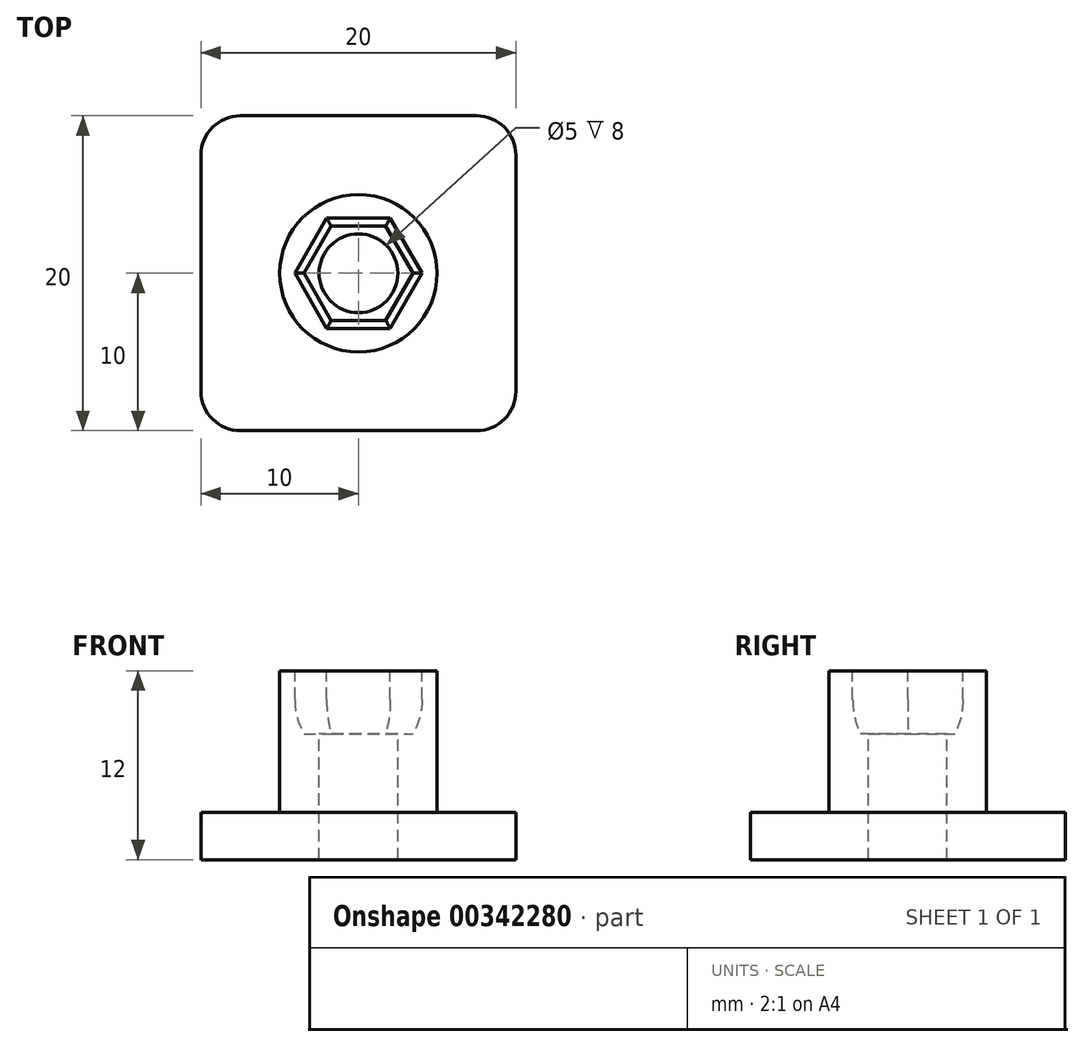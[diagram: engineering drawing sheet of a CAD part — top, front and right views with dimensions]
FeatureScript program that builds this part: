
annotation { "Feature Type Name" : "Feature", "Feature Type Description" : "" }
export const myFeature = defineFeature(function(context is Context, id is Id, definition is map)
    precondition{}
    {
        {
            var Q0;
            Q0=qCreatedBy(makeId("Top.planeOp"),FACE);
            var sketch = newSketch(context, id + "F0", { "sketchPlane" : qUnion([Q0])});
            skLineSegment(sketch, "E0.bottom", {"start": v(7.5, 10) * mm, "end": v(-7.5, 10) * mm});
            skLineSegment(sketch, "E0.top", {"start": v(7.5, -10) * mm, "end": v(-7.5, -10) * mm});
            skLineSegment(sketch, "E0.left", {"start": v(10, 7.5) * mm, "end": v(10, -7.5) * mm});
            skLineSegment(sketch, "E0.right", {"start": v(-10, 7.5) * mm, "end": v(-10, -7.5) * mm});
            skPoint(sketch, "E0.middle", {"position": v(0, 0) * mm});
            skPoint(sketch, "E1.visualSharp", {"position": v(-10, 10) * mm});
            skArc(sketch, "E1.filletArc", {"start": v(-7.5, 10) * mm, "mid": v(-9.27, 9.27) * mm, "end": v(-10, 7.5) * mm});
            skPoint(sketch, "E2.visualSharp", {"position": v(10, 10) * mm});
            skArc(sketch, "E2.filletArc", {"start": v(10, 7.5) * mm, "mid": v(9.27, 9.27) * mm, "end": v(7.5, 10) * mm});
            skPoint(sketch, "E3.visualSharp", {"position": v(10, -10) * mm});
            skArc(sketch, "E3.filletArc", {"start": v(7.5, -10) * mm, "mid": v(9.27, -9.27) * mm, "end": v(10, -7.5) * mm});
            skPoint(sketch, "E4.visualSharp", {"position": v(-10, -10) * mm});
            skArc(sketch, "E4.filletArc", {"start": v(-10, -7.5) * mm, "mid": v(-9.27, -9.27) * mm, "end": v(-7.5, -10) * mm});
            skSolve(sketch);
        }
        {
            var Q0;
            Q0=makeQuery(id+"F0.imprint","IMPRINT",FACE,{"disambiguationData":[TD([[makeQuery(id+"F0.imprint","IMPRINT",EDGE,{"derivedFrom":sQuery(id+"F0.wireOp",EDGE,"E0.bottom")}),1.0]])]});
            extrude(context, id + "F1", {"entities" : qUnion([Q0]), "depth" : 3 * mm});
        }
        {
            var Q0;
            Q0=makeQuery(id+"F1.opExtrude","CAP_FACE",FACE,{"disambiguationData":[OSD([sQuery(id+"F0.wireOp",EDGE,"E0.bottom"),sQuery(id+"F0.wireOp",EDGE,"E0.top"),sQuery(id+"F0.wireOp",EDGE,"E0.left"),sQuery(id+"F0.wireOp",EDGE,"E0.right"),sQuery(id+"F0.wireOp",EDGE,"E1.filletArc"),sQuery(id+"F0.wireOp",EDGE,"E2.filletArc"),sQuery(id+"F0.wireOp",EDGE,"E3.filletArc"),sQuery(id+"F0.wireOp",EDGE,"E4.filletArc")])],"isStart":false});
            var sketch = newSketch(context, id + "F2", { "sketchPlane" : qUnion([Q0])});
            skCircle(sketch, "E5", {"center": v(0, 0) * mm, "radius": 5 * mm});
            skSolve(sketch);
        }
        {
            var Q0;
            Q0=makeQuery(id+"F2.imprint","IMPRINT",FACE,{"disambiguationData":[TD([[makeQuery(id+"F2.imprint","IMPRINT",EDGE,{"derivedFrom":sQuery(id+"F2.wireOp",EDGE,"E5")}),1.0]])]});
            extrude(context, id + "F3", {"entities" : qUnion([Q0]), "operationType" : NewBodyOperationType.ADD, "depth" : 9 * mm});
        }
        {
            var Q0;
            Q0=makeQuery(id+"F3.opExtrude","CAP_FACE",FACE,{"disambiguationData":[OSD([sQuery(id+"F2.wireOp",EDGE,"E5")])],"isStart":false});
            var sketch = newSketch(context, id + "F4", { "sketchPlane" : qUnion([Q0])});
            skCircle(sketch, "E6.cCircle", {"center": v(0, 0) * mm, "radius": 3.5 * mm, "construction": true});
            skLineSegment(sketch, "E6.0", {"start": v(-2.02, 3.5) * mm, "end": v(2.02, 3.5) * mm});
            skLineSegment(sketch, "E6.1", {"start": v(2.02, 3.5) * mm, "end": v(4.04, 0) * mm});
            skLineSegment(sketch, "E6.2", {"start": v(4.04, 0) * mm, "end": v(2.02, -3.5) * mm});
            skLineSegment(sketch, "E6.3", {"start": v(2.02, -3.5) * mm, "end": v(-2.02, -3.5) * mm});
            skLineSegment(sketch, "E6.4", {"start": v(-2.02, -3.5) * mm, "end": v(-4.04, 0) * mm});
            skLineSegment(sketch, "E6.5", {"start": v(-4.04, 0) * mm, "end": v(-2.02, 3.5) * mm});
            skPoint(sketch, "E6.0.midPoint", {"position": v(0, 3.5) * mm});
            skSolve(sketch);
        }
        {
            var Q0;
            Q0=makeQuery(id+"F4.imprint","IMPRINT",FACE,{"disambiguationData":[TD([[makeQuery(id+"F4.imprint","IMPRINT",EDGE,{"derivedFrom":sQuery(id+"F4.wireOp",EDGE,"E6.0")}),-1.0]])]});
            extrude(context, id + "F5", {"entities" : qUnion([Q0]), "operationType" : NewBodyOperationType.REMOVE, "oppositeDirection" : true, "depth" : 4 * mm});
        }
        {
            var Q0;
            Q0=makeQuery(id+"F5.boolean.opBoolean","COPY",FACE,{"derivedFrom":makeQuery(id+"F5.opExtrude","CAP_FACE",FACE,{"disambiguationData":[OSD([sQuery(id+"F4.wireOp",EDGE,"E6.0"),sQuery(id+"F4.wireOp",EDGE,"E6.1"),sQuery(id+"F4.wireOp",EDGE,"E6.2"),sQuery(id+"F4.wireOp",EDGE,"E6.3"),sQuery(id+"F4.wireOp",EDGE,"E6.4"),sQuery(id+"F4.wireOp",EDGE,"E6.5")])],"isStart":false})});
            var sketch = newSketch(context, id + "F6", { "sketchPlane" : qUnion([Q0])});
            skCircle(sketch, "E7", {"center": v(0, 0) * mm, "radius": 2.5 * mm});
            skSolve(sketch);
        }
        {
            var Q0;
            Q0 = qSketchRegion(id + "F6", true);
            extrude(context, id + "F7", {"entities" : qUnion([Q0]), "operationType" : NewBodyOperationType.REMOVE, "oppositeDirection" : true, "depth" : 25 * mm});
        }
        {
            var Q0;
            Q0=makeQuery(id+"F5.boolean.opBoolean","COPY",EDGE,{"derivedFrom":makeQuery(id+"F5.opExtrude","CAP_EDGE",EDGE,{"disambiguationData":[OSD([sQuery(id+"F4.wireOp",EDGE,"E6.4")])],"isStart":false})});
            var Q1;
            Q1=makeQuery(id+"F5.boolean.opBoolean","COPY",EDGE,{"derivedFrom":makeQuery(id+"F5.opExtrude","CAP_EDGE",EDGE,{"disambiguationData":[OSD([sQuery(id+"F4.wireOp",EDGE,"E6.5")])],"isStart":false})});
            var Q2;
            Q2=makeQuery(id+"F5.boolean.opBoolean","COPY",EDGE,{"derivedFrom":makeQuery(id+"F5.opExtrude","CAP_EDGE",EDGE,{"disambiguationData":[OSD([sQuery(id+"F4.wireOp",EDGE,"E6.0")])],"isStart":false})});
            var Q3;
            Q3=makeQuery(id+"F5.boolean.opBoolean","COPY",EDGE,{"derivedFrom":makeQuery(id+"F5.opExtrude","CAP_EDGE",EDGE,{"disambiguationData":[OSD([sQuery(id+"F4.wireOp",EDGE,"E6.1")])],"isStart":false})});
            var Q4;
            Q4=makeQuery(id+"F5.boolean.opBoolean","COPY",EDGE,{"derivedFrom":makeQuery(id+"F5.opExtrude","CAP_EDGE",EDGE,{"disambiguationData":[OSD([sQuery(id+"F4.wireOp",EDGE,"E6.2")])],"isStart":false})});
            var Q5;
            Q5=makeQuery(id+"F5.boolean.opBoolean","COPY",EDGE,{"derivedFrom":makeQuery(id+"F5.opExtrude","CAP_EDGE",EDGE,{"disambiguationData":[OSD([sQuery(id+"F4.wireOp",EDGE,"E6.3")])],"isStart":false})});
            chamfer(context, id + "F8", {"entities" : qUnion([Q0, Q1, Q2, Q3, Q4, Q5]), "chamferType" : ChamferType.TWO_OFFSETS, "width1" : 0.2 * mm, "oppositeDirection" : false, "width2" : 0.5 * mm, "tangentPropagation" : true});
        }
        {
            var Q0;
            {var subQ0=sQuery(id+"F4.wireOp",EDGE,"E6.4");Q0=makeQuery(id+"F8.opChamfer","BLEND_EDGE",EDGE,{"blendedFrom":[makeQuery(id+"F5.boolean.opBoolean","COPY",EDGE,{"derivedFrom":makeQuery(id+"F5.opExtrude","CAP_EDGE",EDGE,{"disambiguationData":[OSD([subQ0])],"isStart":false})}),makeQuery(id+"F5.boolean.opBoolean","COPY",FACE,{"derivedFrom":makeQuery(id+"F5.opExtrude","SWEPT_FACE",FACE,{"disambiguationData":[OSD([subQ0])]})})],"blendedInto":[makeQuery(id+"F5.boolean.opBoolean","COPY",FACE,{"derivedFrom":makeQuery(id+"F5.opExtrude","SWEPT_FACE",FACE,{"disambiguationData":[OSD([subQ0])]})})]});}
            var Q1;
            {var subQ0=sQuery(id+"F4.wireOp",EDGE,"E6.5");Q1=makeQuery(id+"F8.opChamfer","BLEND_EDGE",EDGE,{"blendedFrom":[makeQuery(id+"F5.boolean.opBoolean","COPY",EDGE,{"derivedFrom":makeQuery(id+"F5.opExtrude","CAP_EDGE",EDGE,{"disambiguationData":[OSD([subQ0])],"isStart":false})}),makeQuery(id+"F5.boolean.opBoolean","COPY",FACE,{"derivedFrom":makeQuery(id+"F5.opExtrude","SWEPT_FACE",FACE,{"disambiguationData":[OSD([subQ0])]})})],"blendedInto":[makeQuery(id+"F5.boolean.opBoolean","COPY",FACE,{"derivedFrom":makeQuery(id+"F5.opExtrude","SWEPT_FACE",FACE,{"disambiguationData":[OSD([subQ0])]})})]});}
            var Q2;
            {var subQ0=sQuery(id+"F4.wireOp",EDGE,"E6.3");Q2=makeQuery(id+"F8.opChamfer","BLEND_EDGE",EDGE,{"blendedFrom":[makeQuery(id+"F5.boolean.opBoolean","COPY",EDGE,{"derivedFrom":makeQuery(id+"F5.opExtrude","CAP_EDGE",EDGE,{"disambiguationData":[OSD([subQ0])],"isStart":false})}),makeQuery(id+"F5.boolean.opBoolean","COPY",FACE,{"derivedFrom":makeQuery(id+"F5.opExtrude","SWEPT_FACE",FACE,{"disambiguationData":[OSD([subQ0])]})})],"blendedInto":[makeQuery(id+"F5.boolean.opBoolean","COPY",FACE,{"derivedFrom":makeQuery(id+"F5.opExtrude","SWEPT_FACE",FACE,{"disambiguationData":[OSD([subQ0])]})})]});}
            var Q3;
            {var subQ0=sQuery(id+"F4.wireOp",EDGE,"E6.2");Q3=makeQuery(id+"F8.opChamfer","BLEND_EDGE",EDGE,{"blendedFrom":[makeQuery(id+"F5.boolean.opBoolean","COPY",EDGE,{"derivedFrom":makeQuery(id+"F5.opExtrude","CAP_EDGE",EDGE,{"disambiguationData":[OSD([subQ0])],"isStart":false})}),makeQuery(id+"F5.boolean.opBoolean","COPY",FACE,{"derivedFrom":makeQuery(id+"F5.opExtrude","SWEPT_FACE",FACE,{"disambiguationData":[OSD([subQ0])]})})],"blendedInto":[makeQuery(id+"F5.boolean.opBoolean","COPY",FACE,{"derivedFrom":makeQuery(id+"F5.opExtrude","SWEPT_FACE",FACE,{"disambiguationData":[OSD([subQ0])]})})]});}
            var Q4;
            {var subQ0=sQuery(id+"F4.wireOp",EDGE,"E6.1");Q4=makeQuery(id+"F8.opChamfer","BLEND_EDGE",EDGE,{"blendedFrom":[makeQuery(id+"F5.boolean.opBoolean","COPY",EDGE,{"derivedFrom":makeQuery(id+"F5.opExtrude","CAP_EDGE",EDGE,{"disambiguationData":[OSD([subQ0])],"isStart":false})}),makeQuery(id+"F5.boolean.opBoolean","COPY",FACE,{"derivedFrom":makeQuery(id+"F5.opExtrude","SWEPT_FACE",FACE,{"disambiguationData":[OSD([subQ0])]})})],"blendedInto":[makeQuery(id+"F5.boolean.opBoolean","COPY",FACE,{"derivedFrom":makeQuery(id+"F5.opExtrude","SWEPT_FACE",FACE,{"disambiguationData":[OSD([subQ0])]})})]});}
            var Q5;
            {var subQ0=sQuery(id+"F4.wireOp",EDGE,"E6.0");Q5=makeQuery(id+"F8.opChamfer","BLEND_EDGE",EDGE,{"blendedFrom":[makeQuery(id+"F5.boolean.opBoolean","COPY",EDGE,{"derivedFrom":makeQuery(id+"F5.opExtrude","CAP_EDGE",EDGE,{"disambiguationData":[OSD([subQ0])],"isStart":false})}),makeQuery(id+"F5.boolean.opBoolean","COPY",FACE,{"derivedFrom":makeQuery(id+"F5.opExtrude","SWEPT_FACE",FACE,{"disambiguationData":[OSD([subQ0])]})})],"blendedInto":[makeQuery(id+"F5.boolean.opBoolean","COPY",FACE,{"derivedFrom":makeQuery(id+"F5.opExtrude","SWEPT_FACE",FACE,{"disambiguationData":[OSD([subQ0])]})})]});}
            fillet(context, id + "F9", {"entities" : qUnion([Q0, Q1, Q2, Q3, Q4, Q5]), "radius" : 5 * mm, "tangentPropagation" : true, "allowEdgeOverflow" : false});
        }
    });
